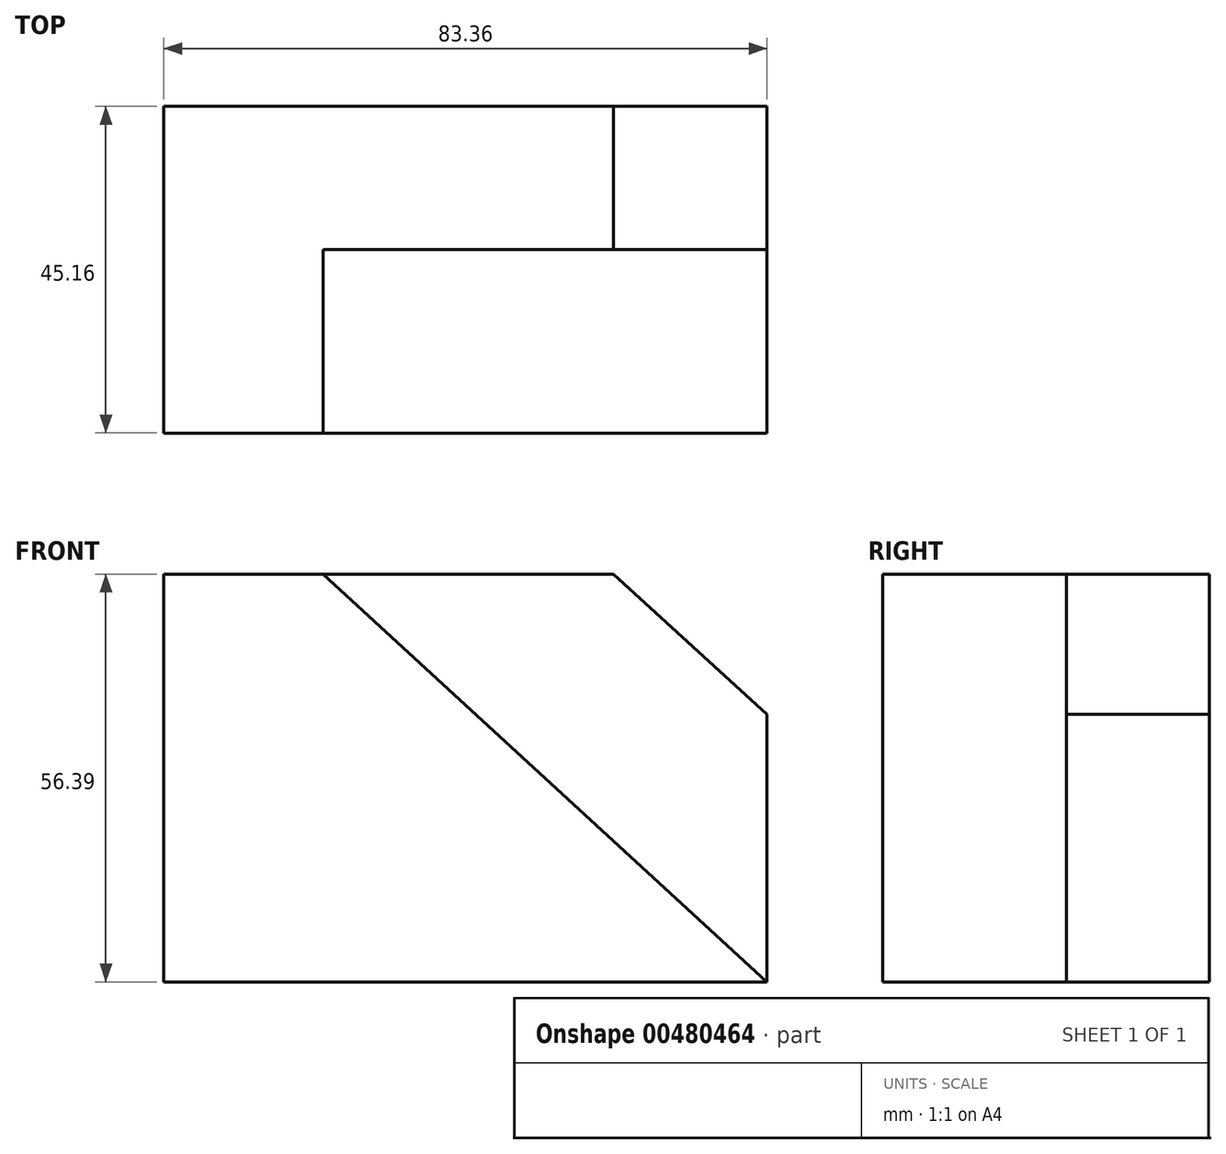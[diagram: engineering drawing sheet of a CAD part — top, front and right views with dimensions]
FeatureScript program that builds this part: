
annotation { "Feature Type Name" : "Feature", "Feature Type Description" : "" }
export const myFeature = defineFeature(function(context is Context, id is Id, definition is map)
    precondition{}
    {
        {
            var Q0;
            Q0=qCreatedBy(makeId("Top.planeOp"),FACE);
            var sketch = newSketch(context, id + "F0", { "sketchPlane" : qUnion([Q0])});
            skLineSegment(sketch, "E0.bottom", {"start": v(-41.68, 22.58) * mm, "end": v(41.68, 22.58) * mm});
            skLineSegment(sketch, "E0.top", {"start": v(-41.68, -22.58) * mm, "end": v(41.68, -22.58) * mm});
            skLineSegment(sketch, "E0.left", {"start": v(-41.68, 22.58) * mm, "end": v(-41.68, -22.58) * mm});
            skLineSegment(sketch, "E0.right", {"start": v(41.68, 22.58) * mm, "end": v(41.68, -22.58) * mm});
            skPoint(sketch, "E0.middle", {"position": v(0, 0) * mm});
            skSolve(sketch);
        }
        {
            var Q0;
            Q0=makeQuery(id+"F0.imprint","IMPRINT",FACE,{"disambiguationData":[TD([[makeQuery(id+"F0.imprint","IMPRINT",EDGE,{"derivedFrom":sQuery(id+"F0.wireOp",EDGE,"E0.bottom")}),-1.0]])]});
            extrude(context, id + "F1", {"entities" : qUnion([Q0]), "depth" : 56.4 * mm});
        }
        {
            var Q0;
            Q0=makeQuery(id+"F1.opExtrude","SWEPT_FACE",FACE,{"disambiguationData":[OSD([sQuery(id+"F0.wireOp",EDGE,"E0.top")])]});
            var sketch = newSketch(context, id + "F2", { "sketchPlane" : qUnion([Q0])});
            skLineSegment(sketch, "E1", {"start": v(-19.65, 56.39) * mm, "end": v(41.68, 0) * mm});
            skLineSegment(sketch, "E2", {"start": v(41.68, 0) * mm, "end": v(41.68, 56.39) * mm});
            skLineSegment(sketch, "E3", {"start": v(41.68, 56.39) * mm, "end": v(-19.65, 56.39) * mm});
            skSolve(sketch);
        }
        {
            var Q0;
            Q0=makeQuery(id+"F2.imprint","IMPRINT",FACE,{"disambiguationData":[TD([[makeQuery(id+"F2.imprint","IMPRINT",EDGE,{"derivedFrom":sQuery(id+"F2.wireOp",EDGE,"E1")}),1.0]])]});
            extrude(context, id + "F3", {"entities" : qUnion([Q0]), "operationType" : NewBodyOperationType.REMOVE, "oppositeDirection" : true, "depth" : 25.4 * mm});
        }
        {
            var Q0;
            Q0=makeQuery(id+"F3.boolean.opBoolean","COPY",FACE,{"derivedFrom":makeQuery(id+"F3.opExtrude","CAP_FACE",FACE,{"disambiguationData":[OSD([sQuery(id+"F2.wireOp",EDGE,"E1"),sQuery(id+"F2.wireOp",EDGE,"E2"),sQuery(id+"F2.wireOp",EDGE,"E3")])],"isStart":false})});
            var sketch = newSketch(context, id + "F4", { "sketchPlane" : qUnion([Q0])});
            skPoint(sketch, "E4", {"position": v(41.68, 37.02) * mm});
            skPoint(sketch, "E5", {"position": v(20.5, 56.39) * mm});
            skLineSegment(sketch, "E6", {"start": v(20.5, 56.39) * mm, "end": v(41.68, 37.02) * mm});
            skSolve(sketch);
        }
        {
            var Q0;
            {var subQ0=sQuery(id+"F4.wireOp",EDGE,"E6");Q0=makeQuery(id+"F4.imprint","IMPRINT",FACE,{"disambiguationData":[TD([[makeQuery(id+"F4.imprint","IMPRINT",EDGE,{"derivedFrom":subQ0}),1.0]])]});}
            extrude(context, id + "F5", {"entities" : qUnion([Q0]), "operationType" : NewBodyOperationType.REMOVE, "oppositeDirection" : true, "depth" : 25.4 * mm});
        }
    });
